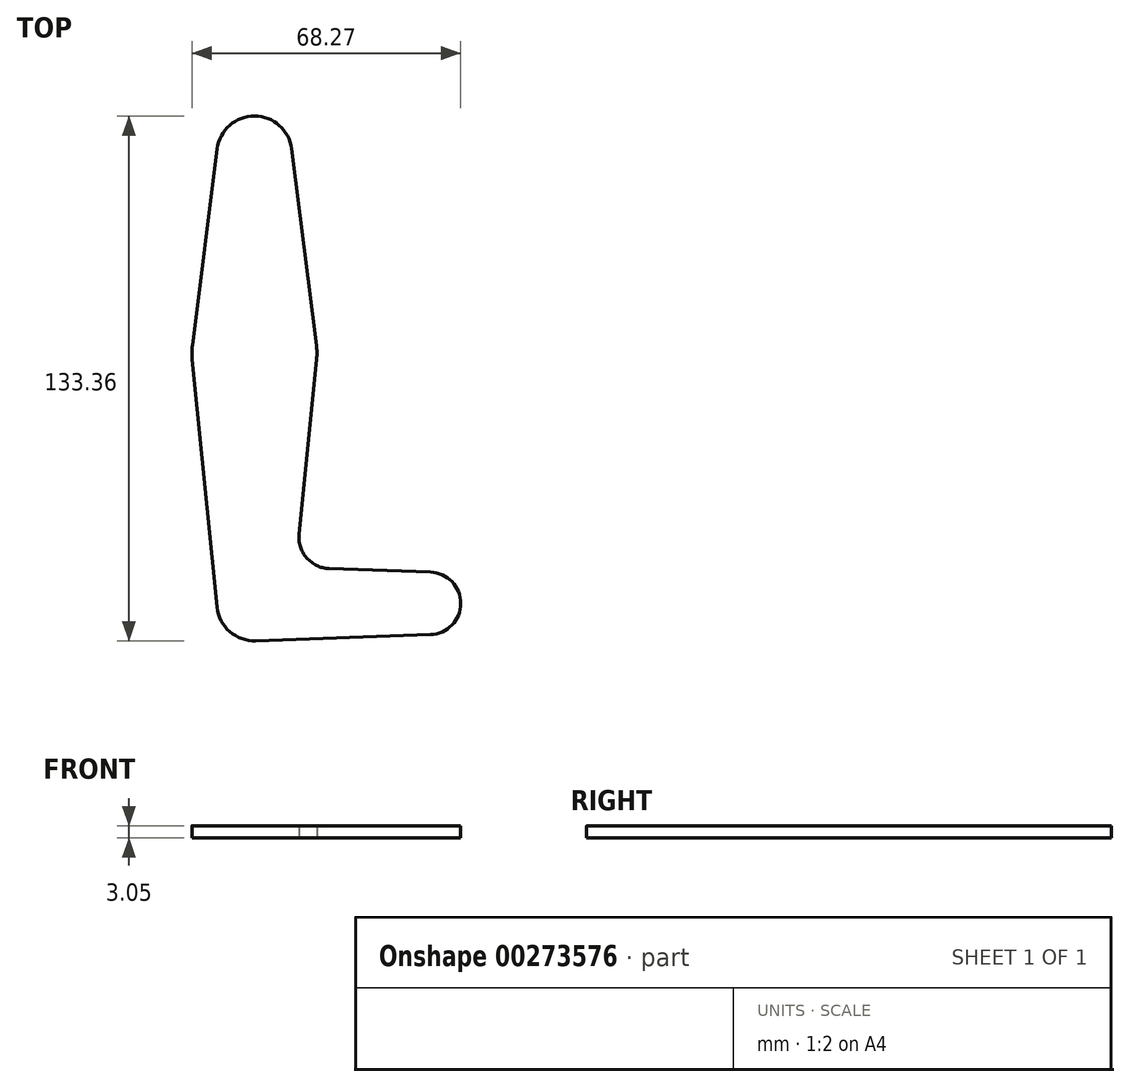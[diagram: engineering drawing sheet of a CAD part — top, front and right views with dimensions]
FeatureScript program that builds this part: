
annotation { "Feature Type Name" : "Feature", "Feature Type Description" : "" }
export const myFeature = defineFeature(function(context is Context, id is Id, definition is map)
    precondition{}
    {
        {
            var Q0;
            Q0=qCreatedBy(makeId("Top.planeOp"),FACE);
            var sketch = newSketch(context, id + "F0", { "sketchPlane" : qUnion([Q0])});
            skCircle(sketch, "E0", {"center": v(0, 0) * mm, "radius": 9.53 * mm});
            skLineSegment(sketch, "E1", {"start": v(0, 0) * mm, "end": v(44.46, 0) * mm, "construction": true});
            skCircle(sketch, "E2", {"center": v(44.46, 0) * mm, "radius": 7.94 * mm});
            skLineSegment(sketch, "E3", {"start": v(0, 0) * mm, "end": v(0, 63.5) * mm, "construction": true});
            skCircle(sketch, "E4", {"center": v(0, 63.5) * mm, "radius": 15.88 * mm});
            skLineSegment(sketch, "E5", {"start": v(0, 63.5) * mm, "end": v(0, 114.3) * mm, "construction": true});
            skCircle(sketch, "E6", {"center": v(0, 114.3) * mm, "radius": 9.53 * mm});
            skLineSegment(sketch, "E7", {"start": v(9.45, 115.5) * mm, "end": v(15.75, 65.48) * mm});
            skLineSegment(sketch, "E8", {"start": v(-9.45, 115.5) * mm, "end": v(-15.75, 65.48) * mm});
            skLineSegment(sketch, "E9", {"start": v(-15.8, 61.91) * mm, "end": v(-9.48, -0.95) * mm});
            skLineSegment(sketch, "E10", {"start": v(11.34, 17.6) * mm, "end": v(15.8, 61.91) * mm});
            skLineSegment(sketch, "E11", {"start": v(18.97, 8.85) * mm, "end": v(44.74, 7.93) * mm});
            skLineSegment(sketch, "E12", {"start": v(0.34, -9.52) * mm, "end": v(44.74, -7.93) * mm});
            skCircle(sketch, "E13", {"center": v(0, 0) * mm, "radius": 3.18 * mm});
            skCircle(sketch, "E14", {"center": v(44.46, 0) * mm, "radius": 3.18 * mm});
            skCircle(sketch, "E15", {"center": v(0, 63.5) * mm, "radius": 3.18 * mm});
            skCircle(sketch, "E16", {"center": v(0, 114.3) * mm, "radius": 3.18 * mm});
            skArc(sketch, "E17.filletArc", {"start": v(11.34, 17.6) * mm, "mid": v(13.26, 11.57) * mm, "end": v(18.97, 8.85) * mm});
            skCircle(sketch, "E18", {"center": v(-3.18, 100.03) * mm, "radius": 3.18 * mm});
            skSolve(sketch);
        }
        {
            var Q0;
            Q0=makeQuery(id+"F0.imprint","IMPRINT",FACE,{"disambiguationData":[TD([[makeQuery(id+"F0.imprint","IMPRINT",EDGE,{"derivedFrom":sQuery(id+"F0.wireOp",EDGE,"E16")}),-1.0]])]});
            var Q1;
            {var subQ1=sQuery(id+"F0.wireOp",EDGE,"E7");Q1=makeQuery(id+"F0.imprint","IMPRINT",FACE,{"disambiguationData":[TD([[makeQuery(id+"F0.imprint","IMPRINT",EDGE,{"derivedFrom":subQ1}),-1.0]])]});}
            var Q2;
            Q2=makeQuery(id+"F0.imprint","IMPRINT",FACE,{"disambiguationData":[TD([[makeQuery(id+"F0.imprint","IMPRINT",EDGE,{"derivedFrom":sQuery(id+"F0.wireOp",EDGE,"E15")}),-1.0]])]});
            var Q3;
            {var subQ0=sQuery(id+"F0.wireOp",EDGE,"E9");Q3=makeQuery(id+"F0.imprint","IMPRINT",FACE,{"disambiguationData":[TD([[makeQuery(id+"F0.imprint","IMPRINT",EDGE,{"derivedFrom":subQ0}),1.0]])]});}
            var Q4;
            Q4=makeQuery(id+"F0.imprint","IMPRINT",FACE,{"disambiguationData":[TD([[makeQuery(id+"F0.imprint","IMPRINT",EDGE,{"derivedFrom":sQuery(id+"F0.wireOp",EDGE,"E13")}),-1.0]])]});
            var Q5;
            Q5=makeQuery(id+"F0.imprint","IMPRINT",FACE,{"disambiguationData":[TD([[makeQuery(id+"F0.imprint","IMPRINT",EDGE,{"derivedFrom":sQuery(id+"F0.wireOp",EDGE,"E14")}),-1.0]])]});
            var Q6;
            Q6=makeQuery(id+"F0.imprint","IMPRINT",FACE,{"disambiguationData":[TD([[makeQuery(id+"F0.imprint","IMPRINT",EDGE,{"derivedFrom":sQuery(id+"F0.wireOp",EDGE,"E14")}),1.0]])]});
            var Q7;
            Q7=makeQuery(id+"F0.imprint","IMPRINT",FACE,{"disambiguationData":[TD([[makeQuery(id+"F0.imprint","IMPRINT",EDGE,{"derivedFrom":sQuery(id+"F0.wireOp",EDGE,"E18")}),1.0]])]});
            var Q8;
            Q8=makeQuery(id+"F0.imprint","IMPRINT",FACE,{"disambiguationData":[TD([[makeQuery(id+"F0.imprint","IMPRINT",EDGE,{"derivedFrom":sQuery(id+"F0.wireOp",EDGE,"E15")}),1.0]])]});
            var Q9;
            Q9=makeQuery(id+"F0.imprint","IMPRINT",FACE,{"disambiguationData":[TD([[makeQuery(id+"F0.imprint","IMPRINT",EDGE,{"derivedFrom":sQuery(id+"F0.wireOp",EDGE,"E16")}),1.0]])]});
            var Q10;
            Q10=makeQuery(id+"F0.imprint","IMPRINT",FACE,{"disambiguationData":[TD([[makeQuery(id+"F0.imprint","IMPRINT",EDGE,{"derivedFrom":sQuery(id+"F0.wireOp",EDGE,"E13")}),1.0]])]});
            extrude(context, id + "F1", {"entities" : qUnion([Q0, Q1, Q2, Q3, Q4, Q5, Q6, Q7, Q8, Q9, Q10]), "depth" : 3.05 * mm});
        }
    });
